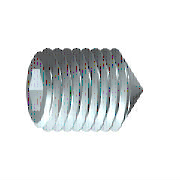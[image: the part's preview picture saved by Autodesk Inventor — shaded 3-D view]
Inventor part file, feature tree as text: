
AUTODESK INVENTOR PART (.ipt)
format: ipt  version: 2017 (Build 210142000, 142)  size: 160,768 bytes
history: native  units: mm (DEFAULTED — no unit token found)
features: sketch x2, extrude x1, other x1, plane x1
ambient origin geometry x8: Origin, YZ Plane, XZ Plane, XY Plane, X Axis, Y Axis, Z Axis, Center Point
bodies: Solid1 (feature_tree), Body (feature_tree)
feature tree (5):
  extrude  "Slot"  TaperAngle=60.0deg  [1 undecoded]
  other  "Work Axis1"
  plane  "Work Plane1"
  sketch  "Sketch1"  dims[d0=2.0mm d1=60.0deg]
  sketch  "Sketch2"  dims[d2=3.0mm d3=1.732051mm d6=90.0deg d4=0.0mm d5=5.0mm d21=10.0mm d7=0.0mm d8=0.866023mm d9=60.0deg d10=0.306725mm d11=60.0deg d12=5.0mm d13=0.0mm d34=0.866023mm d35=0.306725mm d36=0.0mm d37=0.0mm]
note: 1 required parameter value undecoded (feature->parameter linkage not recoverable at this tier; creation-order binding heuristic only, values carry confidence <= 0.55)
